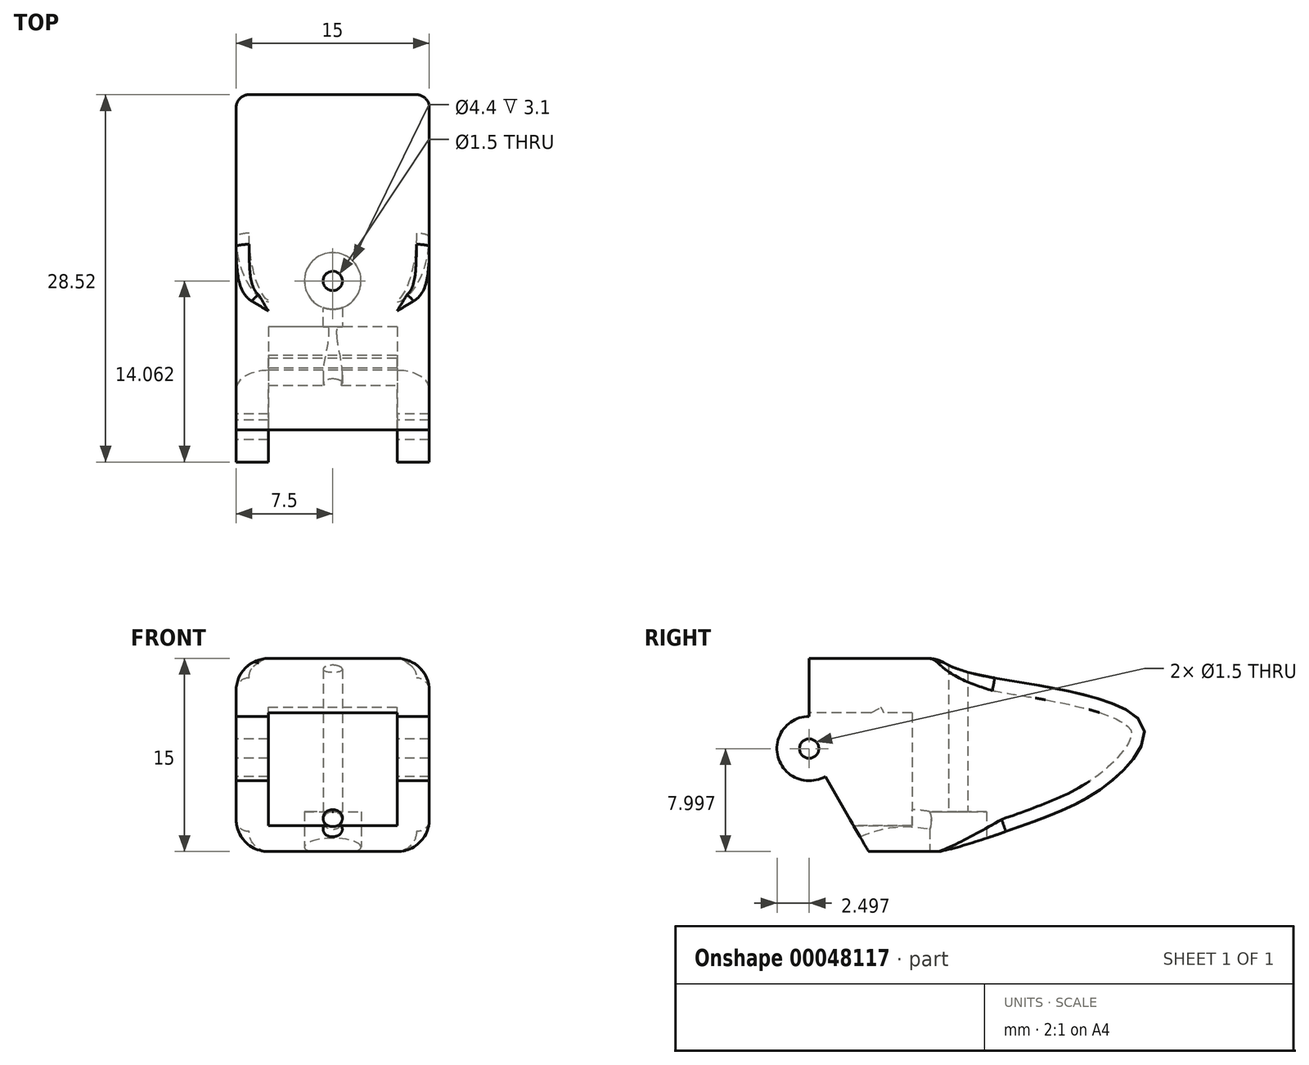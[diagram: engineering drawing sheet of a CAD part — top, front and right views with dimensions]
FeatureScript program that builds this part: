
annotation { "Feature Type Name" : "Feature", "Feature Type Description" : "" }
export const myFeature = defineFeature(function(context is Context, id is Id, definition is map)
    precondition{}
    {
        {
            var Q0;
            Q0=qCreatedBy(makeId("Right.planeOp"),FACE);
            var sketch = newSketch(context, id + "F0", { "sketchPlane" : qUnion([Q0])});
            skLineSegment(sketch, "E0.bottom", {"start": v(-42.54, 1.89) * mm, "end": v(-32.54, 1.89) * mm});
            skLineSegment(sketch, "E0.top", {"start": v(-42.54, -13.11) * mm, "end": v(-32.54, -13.11) * mm});
            skLineSegment(sketch, "E0.left", {"start": v(-42.54, 1.89) * mm, "end": v(-42.54, -13.11) * mm});
            skLineSegment(sketch, "E0.right", {"start": v(-32.54, 1.89) * mm, "end": v(-32.54, -13.11) * mm});
            skCircle(sketch, "E1", {"center": v(-42.54, -5.11) * mm, "radius": 2.5 * mm});
            skCircle(sketch, "E2", {"center": v(-42.54, -5.11) * mm, "radius": 0.75 * mm});
            skLineSegment(sketch, "E3", {"start": v(-42.54, -5.11) * mm, "end": v(-37.92, -13.11) * mm});
            skArc(sketch, "E4", {"start": v(-39.32, -10.69) * mm, "mid": v(-36.32, -6.78) * mm, "end": v(-36.97, -1.9) * mm});
            skLineSegment(sketch, "E5", {"start": v(-42.54, -5.11) * mm, "end": v(-30.42, 1.89) * mm});
            skFitSpline(sketch, "E6", {"points": [v(-32.54, -13.11) * mm, v(-25.27, -10.84) * mm, v(-18.95, -7.53) * mm, v(-16.67, -3.22) * mm, v(-26.87, 0.15) * mm, v(-32.54, 1.89) * mm, v(-34.33, 3.32) * mm, v(-35.98, 1.89) * mm, v(-34.6, -5.39) * mm, v(-35.2, -13.11) * mm, v(-33.28, -13.11) * mm, v(-32.54, -13.11) * mm]});
            skSolve(sketch);
        }
        {
            var Q0;
            {var subQ3=sQuery(id+"F0.wireOp",EDGE,"E0.right");var subQ7=sQuery(id+"F0.wireOp",EDGE,"E0.bottom");var subQ8=makeQuery(id+"F0.imprint","INTERSECT",VERTEX,{"derivedFrom":[subQ7,subQ3]});Q0=makeQuery(id+"F0.imprint","IMPRINT",FACE,{"disambiguationData":[TD([[makeQuery(id+"F0.imprint","IMPRINT",EDGE,{"disambiguationData":[TD([[subQ8,1.0]])],"derivedFrom":subQ7}),-1.0]])]});}
            var Q1;
            {var subQ5=sQuery(id+"F0.wireOp",EDGE,"E0.left");var subQ11=sQuery(id+"F0.wireOp",EDGE,"E0.bottom");var subQ13=makeQuery(id+"F0.imprint","INTERSECT",VERTEX,{"derivedFrom":[subQ11,subQ5]});Q1=makeQuery(id+"F0.imprint","IMPRINT",FACE,{"disambiguationData":[TD([[makeQuery(id+"F0.imprint","IMPRINT",EDGE,{"disambiguationData":[TD([[subQ13,-1.0]])],"derivedFrom":subQ11}),-1.0]])]});}
            var Q2;
            {var subQ3=sQuery(id+"F0.wireOp",EDGE,"E1");var subQ5=sQuery(id+"F0.wireOp",EDGE,"E0.left");var subQ6=makeQuery(id+"F0.imprint","INTERSECT",VERTEX,{"disambiguationData":[OD(1.0)],"derivedFrom":[subQ5,subQ3]});Q2=makeQuery(id+"F0.imprint","IMPRINT",FACE,{"disambiguationData":[TD([[makeQuery(id+"F0.imprint","IMPRINT",EDGE,{"disambiguationData":[TD([[subQ6,1.0]])],"derivedFrom":subQ5}),1.0]])]});}
            var Q3;
            {var subQ1=sQuery(id+"F0.wireOp",EDGE,"E0.left");var subQ4=sQuery(id+"F0.wireOp",EDGE,"E1");var subQ6=makeQuery(id+"F0.imprint","INTERSECT",VERTEX,{"disambiguationData":[OD(0.0)],"derivedFrom":[subQ1,subQ4]});Q3=makeQuery(id+"F0.imprint","IMPRINT",FACE,{"disambiguationData":[TD([[makeQuery(id+"F0.imprint","IMPRINT",EDGE,{"disambiguationData":[TD([[subQ6,-1.0]])],"derivedFrom":subQ1}),-1.0]])]});}
            var Q4;
            {var subQ3=sQuery(id+"F0.wireOp",EDGE,"E1");var subQ5=sQuery(id+"F0.wireOp",EDGE,"E0.left");var subQ7=makeQuery(id+"F0.imprint","INTERSECT",VERTEX,{"disambiguationData":[OD(0.0)],"derivedFrom":[subQ5,subQ3]});Q4=makeQuery(id+"F0.imprint","IMPRINT",FACE,{"disambiguationData":[TD([[makeQuery(id+"F0.imprint","IMPRINT",EDGE,{"disambiguationData":[TD([[subQ7,-1.0]])],"derivedFrom":subQ5}),1.0]])]});}
            var Q5;
            {var subQ0=sQuery(id+"F0.wireOp",EDGE,"E4");Q5=makeQuery(id+"F0.imprint","IMPRINT",FACE,{"disambiguationData":[TD([[makeQuery(id+"F0.imprint","IMPRINT",EDGE,{"derivedFrom":subQ0}),-1.0]])]});}
            var Q6;
            {var subQ3=sQuery(id+"F0.wireOp",EDGE,"E4");Q6=makeQuery(id+"F0.imprint","IMPRINT",FACE,{"disambiguationData":[TD([[makeQuery(id+"F0.imprint","IMPRINT",EDGE,{"derivedFrom":subQ3}),1.0]])]});}
            var Q7;
            {var subQ0=sQuery(id+"F0.wireOp",EDGE,"E5");var subQ3=sQuery(id+"F0.wireOp",EDGE,"E1");var subQ4=makeQuery(id+"F0.imprint","INTERSECT",VERTEX,{"derivedFrom":[subQ3,subQ0]});Q7=makeQuery(id+"F0.imprint","IMPRINT",FACE,{"disambiguationData":[TD([[makeQuery(id+"F0.imprint","IMPRINT",EDGE,{"disambiguationData":[TD([[subQ4,1.0]])],"derivedFrom":subQ3}),1.0]])]});}
            var Q8;
            {var subQ1=sQuery(id+"F0.wireOp",EDGE,"E5");var subQ3=sQuery(id+"F0.wireOp",EDGE,"E0.bottom");var subQ5=makeQuery(id+"F0.imprint","INTERSECT",VERTEX,{"derivedFrom":[subQ3,subQ1]});Q8=makeQuery(id+"F0.imprint","IMPRINT",FACE,{"disambiguationData":[TD([[makeQuery(id+"F0.imprint","IMPRINT",EDGE,{"disambiguationData":[TD([[subQ5,1.0]])],"derivedFrom":subQ3}),-1.0]])]});}
            var Q9;
            {var subQ1=sQuery(id+"F0.wireOp",EDGE,"E0.right");Q9=makeQuery(id+"F0.imprint","IMPRINT",FACE,{"disambiguationData":[TD([[makeQuery(id+"F0.imprint","IMPRINT",EDGE,{"derivedFrom":subQ1}),1.0]])]});}
            var Q10;
            {var subQ0=sQuery(id+"F0.wireOp",EDGE,"2a058fea-8355-4a94-bbbc-ad0f7c4e6a05");var subQ1=sQuery(id+"F0.wireOp",EDGE,"E0.top");var subQ2=makeQuery(id+"F0.imprint","INTERSECT",VERTEX,{"disambiguationData":[OD(1.0)],"derivedFrom":[subQ1,subQ0]});Q10=makeQuery(id+"F0.imprint","IMPRINT",FACE,{"disambiguationData":[TD([[makeQuery(id+"F0.imprint","IMPRINT",EDGE,{"disambiguationData":[TD([[subQ2,-1.0]])],"derivedFrom":subQ1}),1.0]])]});}
            var Q11;
            {var subQ0=sQuery(id+"F0.wireOp",EDGE,"E6");var subQ1=sQuery(id+"F0.wireOp",EDGE,"E0.top");var subQ4=makeQuery(id+"F0.imprint","INTERSECT",VERTEX,{"disambiguationData":[OD(0.0)],"derivedFrom":[subQ1,subQ0]});Q11=makeQuery(id+"F0.imprint","IMPRINT",FACE,{"disambiguationData":[TD([[makeQuery(id+"F0.imprint","IMPRINT",EDGE,{"disambiguationData":[TD([[subQ4,-1.0]])],"derivedFrom":subQ1}),1.0]])]});}
            extrude(context, id + "F1", {"entities" : qUnion([Q0, Q1, Q2, Q3, Q4, Q5, Q6, Q7, Q8, Q9, Q10, Q11]), "depth" : 15 * mm, "symmetric" : true});
        }
        {
            var Q0;
            {var subQ3=sQuery(id+"F0.wireOp",EDGE,"95ba5edd-f1c6-4f5c-9913-7cd7302da014");var subQ5=sQuery(id+"F0.wireOp",EDGE,"E0.right");var subQ6=makeQuery(id+"F0.imprint","INTERSECT",VERTEX,{"disambiguationData":[OD(0.0)],"derivedFrom":[subQ5,subQ3]});Q0=makeQuery(id+"F0.imprint","IMPRINT",FACE,{"disambiguationData":[TD([[makeQuery(id+"F0.imprint","IMPRINT",EDGE,{"disambiguationData":[TD([[subQ6,-1.0]])],"derivedFrom":subQ5}),-1.0]])]});}
            var Q1;
            {var subQ3=sQuery(id+"F0.wireOp",EDGE,"E0.right");var subQ5=sQuery(id+"F0.wireOp",EDGE,"95ba5edd-f1c6-4f5c-9913-7cd7302da014");var subQ7=makeQuery(id+"F0.imprint","INTERSECT",VERTEX,{"disambiguationData":[OD(0.0)],"derivedFrom":[subQ3,subQ5]});Q1=makeQuery(id+"F0.imprint","IMPRINT",FACE,{"disambiguationData":[TD([[makeQuery(id+"F0.imprint","IMPRINT",EDGE,{"disambiguationData":[TD([[subQ7,-1.0]])],"derivedFrom":subQ3}),1.0]])]});}
            var Q2;
            {var subQ1=sQuery(id+"F0.wireOp",EDGE,"93368bc3-3fae-4bae-b1ef-5ce2c96afe8c");var subQ5=sQuery(id+"F0.wireOp",EDGE,"E0.right");var subQ7=makeQuery(id+"F0.imprint","INTERSECT",VERTEX,{"disambiguationData":[OD(1.0)],"derivedFrom":[subQ5,subQ1]});Q2=makeQuery(id+"F0.imprint","IMPRINT",FACE,{"disambiguationData":[TD([[makeQuery(id+"F0.imprint","IMPRINT",EDGE,{"disambiguationData":[TD([[subQ7,-1.0]])],"derivedFrom":subQ5}),1.0]])]});}
            var Q3;
            {var subQ0=sQuery(id+"F0.wireOp",EDGE,"93368bc3-3fae-4bae-b1ef-5ce2c96afe8c");var subQ3=sQuery(id+"F0.wireOp",EDGE,"E0.right");var subQ4=makeQuery(id+"F0.imprint","INTERSECT",VERTEX,{"disambiguationData":[OD(1.0)],"derivedFrom":[subQ3,subQ0]});Q3=makeQuery(id+"F0.imprint","IMPRINT",FACE,{"disambiguationData":[TD([[makeQuery(id+"F0.imprint","IMPRINT",EDGE,{"disambiguationData":[TD([[subQ4,-1.0]])],"derivedFrom":subQ3}),-1.0]])]});}
            var Q4;
            {var subQ3=sQuery(id+"F0.wireOp",EDGE,"E0.right");var subQ5=sQuery(id+"F0.wireOp",EDGE,"95ba5edd-f1c6-4f5c-9913-7cd7302da014");var subQ7=makeQuery(id+"F0.imprint","INTERSECT",VERTEX,{"disambiguationData":[OD(1.0)],"derivedFrom":[subQ3,subQ5]});Q4=makeQuery(id+"F0.imprint","IMPRINT",FACE,{"disambiguationData":[TD([[makeQuery(id+"F0.imprint","IMPRINT",EDGE,{"disambiguationData":[TD([[subQ7,1.0]])],"derivedFrom":subQ5}),-1.0]])]});}
            var Q5;
            {var subQ1=sQuery(id+"F0.wireOp",EDGE,"95ba5edd-f1c6-4f5c-9913-7cd7302da014");var subQ5=sQuery(id+"F0.wireOp",EDGE,"E0.right");var subQ7=makeQuery(id+"F0.imprint","INTERSECT",VERTEX,{"disambiguationData":[OD(1.0)],"derivedFrom":[subQ5,subQ1]});Q5=makeQuery(id+"F0.imprint","IMPRINT",FACE,{"disambiguationData":[TD([[makeQuery(id+"F0.imprint","IMPRINT",EDGE,{"disambiguationData":[TD([[subQ7,-1.0]])],"derivedFrom":subQ1}),-1.0]])]});}
            extrude(context, id + "F2", {"entities" : qUnion([Q0, Q1, Q2, Q3, Q4, Q5]), "operationType" : NewBodyOperationType.ADD, "depth" : 10 * mm, "symmetric" : true});
        }
        {
            var Q0;
            Q0=qCreatedBy(makeId("Right.planeOp"),FACE);
            var sketch = newSketch(context, id + "F3", { "sketchPlane" : qUnion([Q0])});
            skCircle(sketch, "E7", {"center": v(-42.54, -5.11) * mm, "radius": 2.7 * mm});
            skSolve(sketch);
        }
        {
            var Q0;
            Q0=qSketchRegion(id+"F3",true);
            extrude(context, id + "F4", {"entities" : qUnion([Q0]), "operationType" : NewBodyOperationType.REMOVE, "oppositeDirection" : true, "depth" : 10 * mm, "symmetric" : true});
        }
        {
            var Q0;
            {var subQ0=sQuery(id+"F0.wireOp",EDGE,"E0.left");Q0=makeQuery(id+"F1.opExtrude","SWEPT_FACE",FACE,{"disambiguationData":[OSD([subQ0]),TDD([makeQuery(id+"F0.imprint","IMPRINT",EDGE,{"disambiguationData":[TD([[makeQuery(id+"F0.imprint","INTERSECT",VERTEX,{"derivedFrom":[sQuery(id+"F0.wireOp",EDGE,"E0.bottom"),subQ0]}),-1.0]])],"derivedFrom":subQ0})])]});}
            var sketch = newSketch(context, id + "F5", { "sketchPlane" : qUnion([Q0])});
            skLineSegment(sketch, "E8.bottom", {"start": v(5, -2.35) * mm, "end": v(-5, -2.35) * mm});
            skLineSegment(sketch, "E8.top", {"start": v(5, -11.11) * mm, "end": v(-5, -11.11) * mm});
            skLineSegment(sketch, "E8.left", {"start": v(5, -2.35) * mm, "end": v(5, -11.11) * mm});
            skLineSegment(sketch, "E8.right", {"start": v(-5, -2.35) * mm, "end": v(-5, -11.11) * mm});
            skSolve(sketch);
        }
        {
            var Q0;
            Q0=qSketchRegion(id+"F5",true);
            extrude(context, id + "F6", {"entities" : qUnion([Q0]), "operationType" : NewBodyOperationType.REMOVE, "oppositeDirection" : true, "depth" : 8 * mm});
        }
        {
            var Q0;
            {var subQ3=sQuery(id+"F0.wireOp",EDGE,"E4");Q0=makeQuery(id+"F0.imprint","IMPRINT",FACE,{"disambiguationData":[TD([[makeQuery(id+"F0.imprint","IMPRINT",EDGE,{"derivedFrom":subQ3}),1.0]])]});}
            extrude(context, id + "F7", {"entities" : qUnion([Q0]), "operationType" : NewBodyOperationType.REMOVE, "oppositeDirection" : true, "depth" : 10 * mm, "symmetric" : true});
        }
        {
            var Q0;
            Q0=makeQuery(id+"F1.opExtrude","SWEPT_FACE",FACE,{"disambiguationData":[OSD([sQuery(id+"F0.wireOp",EDGE,"E0.top")])]});
            var sketch = newSketch(context, id + "F8", { "sketchPlane" : qUnion([Q0])});
            skCircle(sketch, "E9", {"center": v(0, 30.98) * mm, "radius": 2.2 * mm});
            skPoint(sketch, "E10", {"position": v(0, 32.54) * mm});
            skCircle(sketch, "E11", {"center": v(0, 30.98) * mm, "radius": 0.75 * mm});
            skSolve(sketch);
        }
        {
            var Q0;
            Q0=qSketchRegion(id+"F8",true);
            var Q1;
            Q1=makeQuery(id+"F8.imprint","IMPRINT",FACE,{"disambiguationData":[TD([[makeQuery(id+"F8.imprint","IMPRINT",EDGE,{"derivedFrom":sQuery(id+"F8.wireOp",EDGE,"E11")}),1.0]])]});
            extrude(context, id + "F9", {"entities" : qUnion([Q0, Q1]), "operationType" : NewBodyOperationType.REMOVE, "oppositeDirection" : true, "depth" : 3.1 * mm});
        }
        {
            var Q0;
            Q0=makeQuery(id+"F6.boolean.opBoolean","COPY",FACE,{"derivedFrom":makeQuery(id+"F6.opExtrude","CAP_FACE",FACE,{"disambiguationData":[OSD([sQuery(id+"F5.wireOp",EDGE,"E8.bottom"),sQuery(id+"F5.wireOp",EDGE,"E8.top"),sQuery(id+"F5.wireOp",EDGE,"E8.left"),sQuery(id+"F5.wireOp",EDGE,"E8.right")])],"isStart":false})});
            cPlane(context, id + "F10", {"entities" : qUnion([Q0]), "cplaneType" : CPlaneType.OFFSET, "offset" : 4.54 * mm, "width" : 150 * mm, "height" : 150 * mm});
        }
        {
            var Q0;
            Q0=qCreatedBy(id+"F10.planeOp",FACE);
            var sketch = newSketch(context, id + "F11", { "sketchPlane" : qUnion([Q0])});
            skCircle(sketch, "E12", {"center": v(0, -11.47) * mm, "radius": 0.75 * mm});
            skPoint(sketch, "E13", {"position": v(0, -11.11) * mm});
            skPoint(sketch, "E14", {"position": v(0, -13.1) * mm});
            skSolve(sketch);
        }
        {
            var Q0;
            Q0=qCreatedBy(makeId("Right.planeOp"),FACE);
            var sketch = newSketch(context, id + "F12", { "sketchPlane" : qUnion([Q0])});
            skArc(sketch, "E15", {"start": v(-30.98, -11.47) * mm, "mid": v(-35.03, -10.51) * mm, "end": v(-39.08, -11.47) * mm});
            skSolve(sketch);
        }
        {
            var Q0;
            Q0=qSketchRegion(id+"F11",true);
            var Q1;
            Q1=qConstructionFilter(qBodyType(qCreatedBy(id+"F12",EDGE),BodyType.WIRE),ConstructionObject.NO);
            sweep(context, id + "F13", {"operationType" : NewBodyOperationType.REMOVE, "profiles" : qUnion([Q0]), "path" : qUnion([Q1])});
        }
        {
            var Q0;
            Q0=makeQuery(id+"F1.opExtrude","CAP_EDGE",EDGE,{"disambiguationData":[OSD([sQuery(id+"F0.wireOp",EDGE,"2a058fea-8355-4a94-bbbc-ad0f7c4e6a05")])],"isStart":true});
            var Q1;
            Q1=makeQuery(id+"F1.opExtrude","CAP_EDGE",EDGE,{"disambiguationData":[OSD([sQuery(id+"F0.wireOp",EDGE,"2a058fea-8355-4a94-bbbc-ad0f7c4e6a05")])],"isStart":false});
            var Q2;
            Q2=makeQuery(id+"F1.opExtrude","CAP_EDGE",EDGE,{"disambiguationData":[OSD([sQuery(id+"F0.wireOp",EDGE,"E0.bottom")])],"isStart":true});
            var Q3;
            Q3=makeQuery(id+"F1.opExtrude","CAP_EDGE",EDGE,{"disambiguationData":[OSD([sQuery(id+"F0.wireOp",EDGE,"E0.bottom")])],"isStart":false});
            var Q4;
            Q4=makeQuery(id+"F1.opExtrude","CAP_EDGE",EDGE,{"disambiguationData":[OSD([sQuery(id+"F0.wireOp",EDGE,"E0.top")])],"isStart":true});
            var Q5;
            Q5=makeQuery(id+"F1.opExtrude","CAP_EDGE",EDGE,{"disambiguationData":[OSD([sQuery(id+"F0.wireOp",EDGE,"E0.top")])],"isStart":false});
            var Q6;
            Q6=makeQuery(id+"F1.opExtrude","SWEPT_EDGE",EDGE,{"disambiguationData":[OSD([sQuery(id+"F0.wireOp",EDGE,"E0.bottom"),sQuery(id+"F0.wireOp",EDGE,"E0.right"),sQuery(id+"F0.wireOp",EDGE,"E6")])]});
            fillet(context, id + "F14", {"entities" : qUnion([Q0, Q1, Q2, Q3, Q4, Q5, Q6]), "radius" : 2.5 * mm, "tangentPropagation" : true, "allowEdgeOverflow" : false});
        }
        {
            var Q0;
            {var subQ0=sQuery(id+"F0.wireOp",EDGE,"E0.top");var subQ1=sQuery(id+"F0.wireOp",EDGE,"E6");Q0=makeQuery(id+"F9.boolean.opBoolean","SPLIT",EDGE,{"disambiguationData":[TD([makeQuery(id+"F1.opExtrude","CAP_FACE",FACE,{"disambiguationData":[OSD([sQuery(id+"F0.wireOp",EDGE,"E0.bottom"),subQ0,sQuery(id+"F0.wireOp",EDGE,"E0.left"),sQuery(id+"F0.wireOp",EDGE,"E1"),sQuery(id+"F0.wireOp",EDGE,"E2"),sQuery(id+"F0.wireOp",EDGE,"E3"),subQ1])],"isStart":true})])],"derivedFrom":makeQuery(id+"F1.opExtrude","SWEPT_EDGE",EDGE,{"disambiguationData":[OSD([subQ0,sQuery(id+"F0.wireOp",EDGE,"E0.right"),subQ1])]})});}
            var Q1;
            {var subQ0=sQuery(id+"F0.wireOp",EDGE,"E0.top");var subQ1=sQuery(id+"F0.wireOp",EDGE,"E6");Q1=makeQuery(id+"F9.boolean.opBoolean","SPLIT",EDGE,{"disambiguationData":[TD([makeQuery(id+"F1.opExtrude","CAP_FACE",FACE,{"disambiguationData":[OSD([sQuery(id+"F0.wireOp",EDGE,"E0.bottom"),subQ0,sQuery(id+"F0.wireOp",EDGE,"E0.left"),sQuery(id+"F0.wireOp",EDGE,"E1"),sQuery(id+"F0.wireOp",EDGE,"E2"),sQuery(id+"F0.wireOp",EDGE,"E3"),subQ1])],"isStart":false})])],"derivedFrom":makeQuery(id+"F1.opExtrude","SWEPT_EDGE",EDGE,{"disambiguationData":[OSD([subQ0,sQuery(id+"F0.wireOp",EDGE,"E0.right"),subQ1])]})});}
            var Q2;
            Q2=makeQuery(id+"F1.opExtrude","CAP_EDGE",EDGE,{"disambiguationData":[OSD([sQuery(id+"F0.wireOp",EDGE,"E6")])],"isStart":true});
            var Q3;
            Q3=makeQuery(id+"F1.opExtrude","CAP_EDGE",EDGE,{"disambiguationData":[OSD([sQuery(id+"F0.wireOp",EDGE,"E6")])],"isStart":false});
            var Q4;
            Q4=makeQuery(id+"F14.opFillet","BLEND_EDGE",EDGE,{"blendedFrom":[makeQuery(id+"F1.opExtrude","CAP_EDGE",EDGE,{"disambiguationData":[OSD([sQuery(id+"F0.wireOp",EDGE,"E0.top")])],"isStart":false}),makeQuery(id+"F1.opExtrude","SWEPT_FACE",FACE,{"disambiguationData":[OSD([sQuery(id+"F0.wireOp",EDGE,"E6")])]})],"blendedInto":[makeQuery(id+"F1.opExtrude","SWEPT_FACE",FACE,{"disambiguationData":[OSD([sQuery(id+"F0.wireOp",EDGE,"E6")])]})]});
            var Q5;
            Q5=makeQuery(id+"F14.opFillet","BLEND_EDGE",EDGE,{"blendedFrom":[makeQuery(id+"F1.opExtrude","CAP_EDGE",EDGE,{"disambiguationData":[OSD([sQuery(id+"F0.wireOp",EDGE,"E0.top")])],"isStart":true}),makeQuery(id+"F1.opExtrude","SWEPT_FACE",FACE,{"disambiguationData":[OSD([sQuery(id+"F0.wireOp",EDGE,"E6")])]})],"blendedInto":[makeQuery(id+"F1.opExtrude","SWEPT_FACE",FACE,{"disambiguationData":[OSD([sQuery(id+"F0.wireOp",EDGE,"E6")])]})]});
            fillet(context, id + "F15", {"entities" : qUnion([Q0, Q1, Q2, Q3, Q4, Q5]), "radius" : 1 * mm, "tangentPropagation" : true, "allowEdgeOverflow" : false});
        }
        {
            var Q0;
            Q0=makeQuery(id+"F8.imprint","IMPRINT",FACE,{"disambiguationData":[TD([[makeQuery(id+"F8.imprint","IMPRINT",EDGE,{"derivedFrom":sQuery(id+"F8.wireOp",EDGE,"E11")}),1.0]])]});
            var Q1;
            Q1=sQuery(id+"F8.wireOp",EDGE,"E11");
            extrude(context, id + "F16", {"entities" : qUnion([Q0]), "operationType" : NewBodyOperationType.REMOVE, "surfaceEntities" : qUnion([Q1]), "oppositeDirection" : true, "depth" : 15 * mm});
        }
    });
